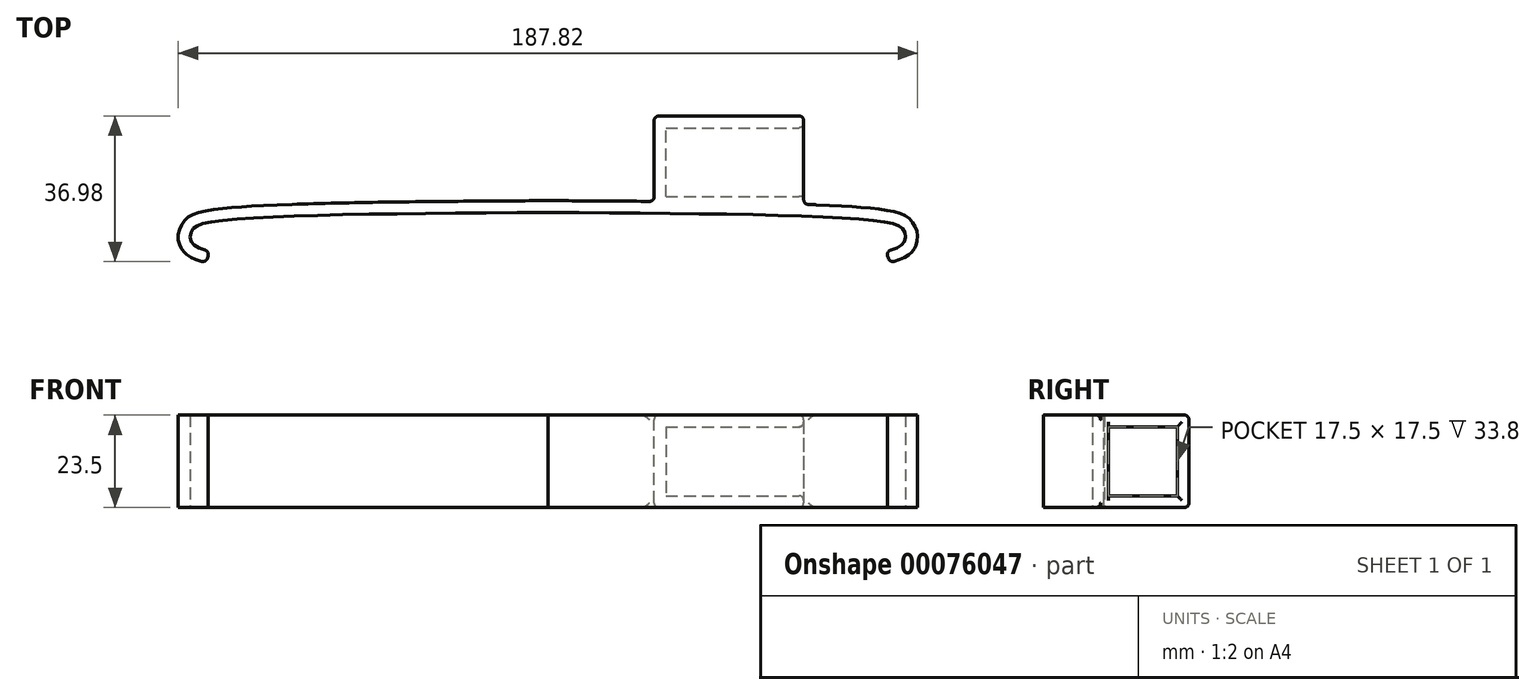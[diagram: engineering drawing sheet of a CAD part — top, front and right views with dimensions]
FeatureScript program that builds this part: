
annotation { "Feature Type Name" : "Feature", "Feature Type Description" : "" }
export const myFeature = defineFeature(function(context is Context, id is Id, definition is map)
    precondition{}
    {
        {
            var Q0;
            Q0=qCreatedBy(makeId("Top.planeOp"),FACE);
            var sketch = newSketch(context, id + "F0", { "sketchPlane" : qUnion([Q0])});
            skLineSegment(sketch, "E0", {"start": v(0, 0) * mm, "end": v(93.82, 0) * mm, "construction": true});
            skLineSegment(sketch, "E1.0", {"start": v(0, -2.5) * mm, "end": v(93.82, -2.5) * mm, "construction": true});
            skLineSegment(sketch, "E2.0", {"start": v(0, -4.7) * mm, "end": v(93.82, -4.7) * mm, "construction": true});
            skLineSegment(sketch, "E3.0", {"start": v(0, -7.7) * mm, "end": v(93.82, -7.7) * mm, "construction": true});
            skLineSegment(sketch, "E4.0", {"start": v(0, -9.9) * mm, "end": v(93.82, -9.9) * mm, "construction": true});
            skLineSegment(sketch, "E5", {"start": v(0, -9.9) * mm, "end": v(0, 27.4) * mm, "construction": true});
            skLineSegment(sketch, "E6.0", {"start": v(90.5, -9.4) * mm, "end": v(90.5, 27.4) * mm, "construction": true});
            skLineSegment(sketch, "E7.0", {"start": v(86, -9.87) * mm, "end": v(86, 27.4) * mm, "construction": true});
            skLineSegment(sketch, "E8.0", {"start": v(75.5, -9.4) * mm, "end": v(75.5, 27.4) * mm, "construction": true});
            skLineSegment(sketch, "E9.0", {"start": v(3, 0) * mm, "end": v(3, 0) * mm});
            skLineSegment(sketch, "E10.0", {"start": v(30, 0) * mm, "end": v(30, 0) * mm});
            skLineSegment(sketch, "E11.0", {"start": v(30, 21.5) * mm, "end": v(65, 21.5) * mm});
            skLineSegment(sketch, "E12.0", {"start": v(27, 24.5) * mm, "end": v(65, 24.5) * mm});
            skLineSegment(sketch, "E13.0", {"start": v(30, 4) * mm, "end": v(65, 4) * mm});
            skLineSegment(sketch, "E14.0", {"start": v(27, 0) * mm, "end": v(27, 0) * mm});
            skLineSegment(sketch, "E15.trimOffspring", {"start": v(27, 2.78) * mm, "end": v(27, 24.5) * mm});
            skLineSegment(sketch, "E16.trimOffspring", {"start": v(30, 2.75) * mm, "end": v(30, 21.5) * mm});
            skFitSpline(sketch, "E17", {"points": [v(0, 0) * mm, v(86, -2.5) * mm, v(90.5, -4.7) * mm, v(90.5, -7.7) * mm, v(86, -9.87) * mm], "startDerivative": vector(187.17, -1.33) * mm, "endDerivative": vector(-39.06, -10.84) * mm});
            skFitSpline(sketch, "E18.0", {"points": [v(0.02, 3) * mm, v(7.82, 2.94) * mm, v(19.52, 2.86) * mm, v(34.42, 2.7) * mm, v(45.06, 2.55) * mm, v(55, 2.35) * mm, v(64.06, 2.1) * mm, v(70.73, 1.82) * mm, v(75.45, 1.56) * mm, v(78.67, 1.34) * mm, v(81.55, 1.1) * mm, v(84.08, 0.83) * mm, v(86.24, 0.52) * mm, v(88.05, 0.17) * mm, v(89.37, -0.22) * mm, v(90.38, -0.65) * mm, v(91.11, -1.05) * mm, v(91.8, -1.56) * mm, v(92.42, -2.18) * mm, v(92.93, -2.88) * mm, v(93.32, -3.6) * mm, v(93.6, -4.35) * mm, v(93.8, -5.14) * mm, v(93.9, -5.97) * mm, v(93.89, -6.84) * mm, v(93.76, -7.59) * mm, v(93.58, -8.2) * mm, v(93.4, -8.66) * mm, v(93.16, -9.12) * mm, v(92.87, -9.56) * mm, v(92.55, -9.96) * mm, v(92.1, -10.42) * mm, v(91.51, -10.9) * mm, v(90.8, -11.33) * mm, v(90.1, -11.67) * mm, v(89.19, -12.05) * mm, v(88.06, -12.41) * mm, v(87.2, -12.65) * mm, v(86.8, -12.76) * mm]});
            skLineSegment(sketch, "E19", {"start": v(86, -9.87) * mm, "end": v(86.8, -12.76) * mm});
            skLineSegment(sketch, "E20.trimOffspring", {"start": v(65, 2.04) * mm, "end": v(65, 24.5) * mm});
            skLineSegment(sketch, "E21", {"start": v(0, 0) * mm, "end": v(0, 3) * mm});
            skLineSegment(sketch, "E22", {"start": v(0, 3) * mm, "end": v(0.02, 3) * mm});
            skSolve(sketch);
        }
        {
            var Q0;
            Q0=makeQuery(id+"F0.imprint","IMPRINT",FACE,{"disambiguationData":[TD([[makeQuery(id+"F0.imprint","IMPRINT",EDGE,{"derivedFrom":sQuery(id+"F0.wireOp",EDGE,"E17")}),1.0]])]});
            extrude(context, id + "F1", {"entities" : qUnion([Q0]), "depth" : 23.5 * mm});
        }
        {
            var Q0;
            Q0=makeQuery(id+"F1.opExtrude","SWEPT_BODY",BODY,{"disambiguationData":[OSD([sQuery(id+"F0.wireOp",EDGE,"E17"),sQuery(id+"F0.wireOp",EDGE,"E18.0"),sQuery(id+"F0.wireOp",EDGE,"E19"),sQuery(id+"F0.wireOp",EDGE,"BnNgbtxA-4QhR-yl19-m1yE-QKepiJJErQsK")])]});
            var Q1;
            Q1=qCreatedBy(makeId("Right.planeOp"),FACE);
            mirror(context, id + "F2", {"operationType" : NewBodyOperationType.ADD, "entities" : qUnion([Q0]), "mirrorPlane" : qUnion([Q1])});
        }
        {
            var Q0;
            {var subQ0=sQuery(id+"F0.wireOp",EDGE,"E13.0");Q0=makeQuery(id+"F0.imprint","IMPRINT",FACE,{"disambiguationData":[TD([[makeQuery(id+"F0.imprint","IMPRINT",EDGE,{"derivedFrom":subQ0}),-1.0]])]});}
            var Q1;
            {var subQ6=sQuery(id+"F0.wireOp",EDGE,"E11.0");Q1=makeQuery(id+"F0.imprint","IMPRINT",FACE,{"disambiguationData":[TD([[makeQuery(id+"F0.imprint","IMPRINT",EDGE,{"derivedFrom":subQ6}),1.0]])]});}
            var Q2;
            Q2=makeQuery(id+"F1.opExtrude","CAP_FACE",FACE,{"disambiguationData":[OSD([sQuery(id+"F0.wireOp",EDGE,"E17"),sQuery(id+"F0.wireOp",EDGE,"E18.0"),sQuery(id+"F0.wireOp",EDGE,"E19"),sQuery(id+"F0.wireOp",EDGE,"BnNgbtxA-4QhR-yl19-m1yE-QKepiJJErQsK")])],"isStart":false});
            extrude(context, id + "F3", {"entities" : qUnion([Q0, Q1]), "operationType" : NewBodyOperationType.ADD, "endBound" : BoundingType.UP_TO_SURFACE, "endBoundEntityFace" : qUnion([Q2]), "depth" : 25 * mm});
        }
        {
            var Q0;
            {var subQ0=sQuery(id+"F0.wireOp",EDGE,"E11.0");Q0=makeQuery(id+"F0.imprint","IMPRINT",FACE,{"disambiguationData":[TD([[makeQuery(id+"F0.imprint","IMPRINT",EDGE,{"derivedFrom":subQ0}),-1.0]])]});}
            extrude(context, id + "F4", {"entities" : qUnion([Q0]), "operationType" : NewBodyOperationType.ADD, "depth" : 3 * mm});
        }
        {
            var Q0;
            {var subQ0=sQuery(id+"F0.wireOp",EDGE,"E18.0");var subQ1=makeQuery(id+"F1.opExtrude","CAP_FACE",FACE,{"disambiguationData":[OSD([sQuery(id+"F0.wireOp",EDGE,"E17"),subQ0,sQuery(id+"F0.wireOp",EDGE,"E19"),sQuery(id+"F0.wireOp",EDGE,"E21"),sQuery(id+"F0.wireOp",EDGE,"E22")])],"isStart":false});Q0=makeQuery(id+"F3.boolean.opBoolean","MERGE",FACE,{"derivedFrom":[makeQuery(id+"F2.boolean.opBoolean","MERGE",FACE,{"derivedFrom":[subQ1,makeQuery(id+"F2.opPattern","COPY",FACE,{"derivedFrom":subQ1,"instanceName":"1"})]}),makeQuery(id+"F3.opExtrude","CAP_FACE",FACE,{"disambiguationData":[OSD([sQuery(id+"F0.wireOp",EDGE,"E11.0"),sQuery(id+"F0.wireOp",EDGE,"E12.0"),sQuery(id+"F0.wireOp",EDGE,"E13.0"),sQuery(id+"F0.wireOp",EDGE,"E15.trimOffspring"),sQuery(id+"F0.wireOp",EDGE,"E16.trimOffspring"),subQ0,sQuery(id+"F0.wireOp",EDGE,"E20.trimOffspring")])],"isStart":false})]});}
            var sketch = newSketch(context, id + "F5", { "sketchPlane" : qUnion([Q0])});
            skLineSegment(sketch, "E23.0", {"start": v(65, 4) * mm, "end": v(65, 21.5) * mm});
            skSolve(sketch);
        }
        {
            var Q0;
            Q0=makeQuery(id+"F5.imprint","IMPRINT",FACE,{"disambiguationData":[TD([[makeQuery(id+"F5.imprint","IMPRINT",EDGE,{"derivedFrom":sQuery(id+"F5.wireOp",EDGE,"E23.0")}),1.0]])]});
            extrude(context, id + "F6", {"entities" : qUnion([Q0]), "operationType" : NewBodyOperationType.ADD, "oppositeDirection" : true, "depth" : 3 * mm});
        }
        {
            var Q0;
            Q0=makeQuery(id+"F3.opExtrude","SWEPT_EDGE",EDGE,{"disambiguationData":[OSD([sQuery(id+"F0.wireOp",EDGE,"E12.0"),sQuery(id+"F0.wireOp",EDGE,"E20.trimOffspring")])]});
            var Q1;
            Q1=makeQuery(id+"F1.opExtrude","SWEPT_EDGE",EDGE,{"disambiguationData":[OSD([sQuery(id+"F0.wireOp",EDGE,"E17"),sQuery(id+"F0.wireOp",EDGE,"E19")])]});
            var Q2;
            Q2=makeQuery(id+"F1.opExtrude","SWEPT_EDGE",EDGE,{"disambiguationData":[OSD([sQuery(id+"F0.wireOp",EDGE,"E18.0"),sQuery(id+"F0.wireOp",EDGE,"E19")])]});
            var Q3;
            {var subQ0=sQuery(id+"F0.wireOp",EDGE,"E20.trimOffspring");Q3=makeQuery(id+"F6.boolean.opBoolean","MERGE",EDGE,{"derivedFrom":[makeQuery(id+"F3.opExtrude","CAP_EDGE",EDGE,{"disambiguationData":[OSD([subQ0]),TDD([makeQuery(id+"F0.imprint","IMPRINT",EDGE,{"disambiguationData":[TD([[makeQuery(id+"F0.imprint","INTERSECT",VERTEX,{"derivedFrom":[sQuery(id+"F0.wireOp",EDGE,"E13.0"),subQ0]}),1.0]])],"derivedFrom":subQ0})])],"isStart":false}),makeQuery(id+"F3.opExtrude","CAP_EDGE",EDGE,{"disambiguationData":[OSD([subQ0]),TDD([makeQuery(id+"F0.imprint","IMPRINT",EDGE,{"disambiguationData":[TD([[makeQuery(id+"F0.imprint","INTERSECT",VERTEX,{"derivedFrom":[sQuery(id+"F0.wireOp",EDGE,"E11.0"),subQ0]}),-1.0]])],"derivedFrom":subQ0})])],"isStart":false}),makeQuery(id+"F6.opExtrude","CAP_EDGE",EDGE,{"disambiguationData":[OSD([sQuery(id+"F5.wireOp",EDGE,"E23.0")])],"isStart":true})]});}
            var Q4;
            Q4=makeQuery(id+"F3.opExtrude","CAP_EDGE",EDGE,{"disambiguationData":[OSD([sQuery(id+"F0.wireOp",EDGE,"E12.0")])],"isStart":false});
            var Q5;
            Q5=makeQuery(id+"F3.opExtrude","CAP_EDGE",EDGE,{"disambiguationData":[OSD([sQuery(id+"F0.wireOp",EDGE,"E15.trimOffspring")])],"isStart":false});
            var Q6;
            Q6=makeQuery(id+"F3.opExtrude","SWEPT_EDGE",EDGE,{"disambiguationData":[OSD([sQuery(id+"F0.wireOp",EDGE,"E12.0"),sQuery(id+"F0.wireOp",EDGE,"E15.trimOffspring")])]});
            var Q7;
            Q7=makeQuery(id+"F3.opExtrude","CAP_EDGE",EDGE,{"disambiguationData":[OSD([sQuery(id+"F0.wireOp",EDGE,"E15.trimOffspring")])],"isStart":true});
            var Q8;
            Q8=makeQuery(id+"F3.opExtrude","CAP_EDGE",EDGE,{"disambiguationData":[OSD([sQuery(id+"F0.wireOp",EDGE,"E12.0")])],"isStart":true});
            var Q9;
            Q9=makeQuery(id+"F6.opExtrude","CAP_EDGE",EDGE,{"disambiguationData":[OSD([sQuery(id+"F5.wireOp",EDGE,"E23.0")])],"isStart":false});
            var Q10;
            Q10=makeQuery(id+"F3.opExtrude","SWEPT_EDGE",EDGE,{"disambiguationData":[OSD([sQuery(id+"F0.wireOp",EDGE,"E11.0"),sQuery(id+"F0.wireOp",EDGE,"E20.trimOffspring")])]});
            var Q11;
            Q11=makeQuery(id+"F4.opExtrude","CAP_EDGE",EDGE,{"disambiguationData":[OSD([sQuery(id+"F0.wireOp",EDGE,"E20.trimOffspring")])],"isStart":false});
            var Q12;
            Q12=makeQuery(id+"F3.opExtrude","SWEPT_EDGE",EDGE,{"disambiguationData":[OSD([sQuery(id+"F0.wireOp",EDGE,"E18.0"),sQuery(id+"F0.wireOp",EDGE,"E20.trimOffspring")])]});
            var Q13;
            Q13=makeQuery(id+"F2.opPattern","COPY",EDGE,{"derivedFrom":makeQuery(id+"F1.opExtrude","SWEPT_EDGE",EDGE,{"disambiguationData":[OSD([sQuery(id+"F0.wireOp",EDGE,"E17"),sQuery(id+"F0.wireOp",EDGE,"E19")])]}),"instanceName":"1"});
            var Q14;
            Q14=makeQuery(id+"F2.opPattern","COPY",EDGE,{"derivedFrom":makeQuery(id+"F1.opExtrude","SWEPT_EDGE",EDGE,{"disambiguationData":[OSD([sQuery(id+"F0.wireOp",EDGE,"E18.0"),sQuery(id+"F0.wireOp",EDGE,"E19")])]}),"instanceName":"1"});
            var Q15;
            {var subQ0=sQuery(id+"F0.wireOp",EDGE,"E20.trimOffspring");Q15=makeQuery(id+"F4.boolean.opBoolean","MERGE",EDGE,{"derivedFrom":[makeQuery(id+"F3.opExtrude","CAP_EDGE",EDGE,{"disambiguationData":[OSD([subQ0]),TDD([makeQuery(id+"F0.imprint","IMPRINT",EDGE,{"disambiguationData":[TD([[makeQuery(id+"F0.imprint","INTERSECT",VERTEX,{"derivedFrom":[sQuery(id+"F0.wireOp",EDGE,"E13.0"),subQ0]}),1.0]])],"derivedFrom":subQ0})])],"isStart":true}),makeQuery(id+"F3.opExtrude","CAP_EDGE",EDGE,{"disambiguationData":[OSD([subQ0]),TDD([makeQuery(id+"F0.imprint","IMPRINT",EDGE,{"disambiguationData":[TD([[makeQuery(id+"F0.imprint","INTERSECT",VERTEX,{"derivedFrom":[sQuery(id+"F0.wireOp",EDGE,"E11.0"),subQ0]}),-1.0]])],"derivedFrom":subQ0})])],"isStart":true}),makeQuery(id+"F4.opExtrude","CAP_EDGE",EDGE,{"disambiguationData":[OSD([subQ0])],"isStart":true})]});}
            var Q16;
            Q16=makeQuery(id+"F3.opExtrude","SWEPT_EDGE",EDGE,{"disambiguationData":[OSD([sQuery(id+"F0.wireOp",EDGE,"E15.trimOffspring"),sQuery(id+"F0.wireOp",EDGE,"E18.0")])]});
            fillet(context, id + "F7", {"entities" : qUnion([Q0, Q1, Q2, Q3, Q4, Q5, Q6, Q7, Q8, Q9, Q10, Q11, Q12, Q13, Q14, Q15, Q16]), "radius" : 1.2 * mm, "allowEdgeOverflow" : false});
        }
    });
